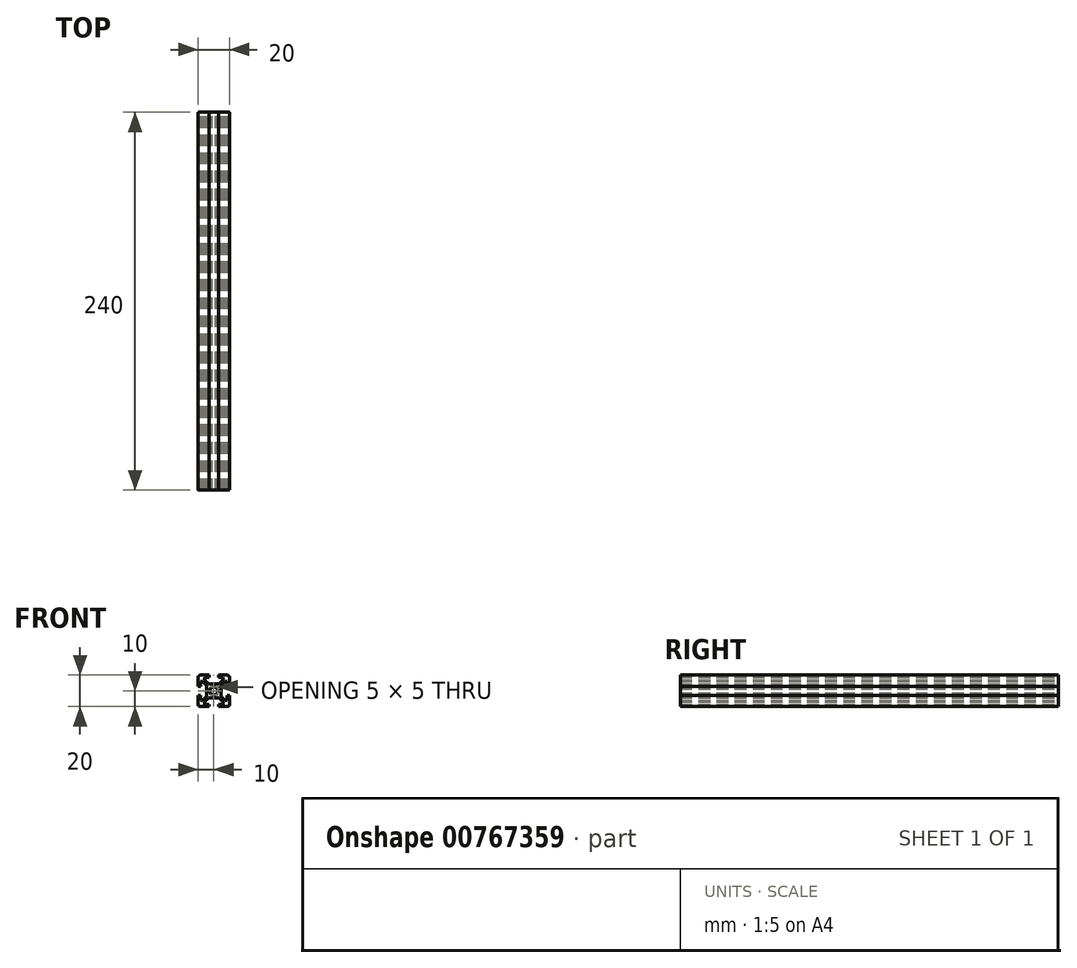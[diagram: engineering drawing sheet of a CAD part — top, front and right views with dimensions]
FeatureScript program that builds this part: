
annotation { "Feature Type Name" : "Feature", "Feature Type Description" : "" }
export const myFeature = defineFeature(function(context is Context, id is Id, definition is map)
    precondition{}
    {
        {
            var Q0;
            Q0=qCreatedBy(makeId("Front.planeOp"),FACE);
            var sketch = newSketch(context, id + "F0", { "sketchPlane" : qUnion([Q0])});
            skLineSegment(sketch, "E0.bottom", {"start": v(8.5, -10) * mm, "end": v(3, -10) * mm});
            skLineSegment(sketch, "E0.top", {"start": v(8.5, 10) * mm, "end": v(3, 10) * mm});
            skLineSegment(sketch, "E0.left", {"start": v(10, -8.5) * mm, "end": v(10, -3) * mm});
            skLineSegment(sketch, "E0.right", {"start": v(-10, -8.5) * mm, "end": v(-10, -3) * mm});
            skPoint(sketch, "E0.middle", {"position": v(0, 0) * mm});
            skLineSegment(sketch, "E1.bottom", {"start": v(6, -8.5) * mm, "end": v(3, -8.5) * mm});
            skLineSegment(sketch, "E1.top", {"start": v(6, 8.5) * mm, "end": v(3, 8.5) * mm});
            skLineSegment(sketch, "E1.left", {"start": v(8.5, -6) * mm, "end": v(8.5, -3) * mm});
            skLineSegment(sketch, "E1.right", {"start": v(-8.5, -6) * mm, "end": v(-8.5, -3) * mm});
            skLineSegment(sketch, "E2.bottom", {"start": v(3.44, -4.5) * mm, "end": v(-3.44, -4.5) * mm});
            skLineSegment(sketch, "E2.top", {"start": v(3.44, 4.5) * mm, "end": v(-3.44, 4.5) * mm});
            skLineSegment(sketch, "E2.left", {"start": v(4.5, -3.44) * mm, "end": v(4.5, 3.44) * mm});
            skLineSegment(sketch, "E2.right", {"start": v(-4.5, -3.44) * mm, "end": v(-4.5, 3.44) * mm});
            skLineSegment(sketch, "E3.bottom", {"start": v(8.5, -6) * mm, "end": v(7.06, -6) * mm});
            skLineSegment(sketch, "E3.top", {"start": v(8.5, 6) * mm, "end": v(7.06, 6) * mm});
            skLineSegment(sketch, "E4.left", {"start": v(6, -8.5) * mm, "end": v(6, -7.06) * mm});
            skLineSegment(sketch, "E4.right", {"start": v(-6, -8.5) * mm, "end": v(-6, -7.06) * mm});
            skPoint(sketch, "E5.orphan", {"position": v(-8.5, 8.5) * mm});
            skPoint(sketch, "E6.orphan", {"position": v(8.5, 8.5) * mm});
            skPoint(sketch, "E7.orphan", {"position": v(8.5, -8.5) * mm});
            skPoint(sketch, "E8.orphan", {"position": v(-8.5, -8.5) * mm});
            skLineSegment(sketch, "E9.trimOffspring", {"start": v(-6, 7.06) * mm, "end": v(-6, 8.5) * mm});
            skLineSegment(sketch, "E10.trimOffspring", {"start": v(-7.06, 6) * mm, "end": v(-8.5, 6) * mm});
            skLineSegment(sketch, "E11.trimOffspring", {"start": v(6, 7.06) * mm, "end": v(6, 8.5) * mm});
            skLineSegment(sketch, "E12.trimOffspring", {"start": v(-7.06, -6) * mm, "end": v(-8.5, -6) * mm});
            skLineSegment(sketch, "E13", {"start": v(-10, 10) * mm, "end": v(0, 0) * mm, "construction": true});
            skLineSegment(sketch, "E14", {"start": v(10, 10) * mm, "end": v(0, 0) * mm, "construction": true});
            skLineSegment(sketch, "E15", {"start": v(-6, 7.06) * mm, "end": v(-3.44, 4.5) * mm});
            skPoint(sketch, "E15.endSnap0", {"position": v(7.25, -6) * mm});
            skLineSegment(sketch, "E16", {"start": v(6, -7.06) * mm, "end": v(3.44, -4.5) * mm});
            skLineSegment(sketch, "E17", {"start": v(7.06, 6) * mm, "end": v(4.5, 3.44) * mm});
            skLineSegment(sketch, "E18", {"start": v(6, 7.06) * mm, "end": v(3.44, 4.5) * mm});
            skPoint(sketch, "E19.orphan", {"position": v(6, -6) * mm});
            skPoint(sketch, "E20.orphan", {"position": v(-4.5, -4.5) * mm});
            skPoint(sketch, "E21.orphan", {"position": v(-4.5, 4.5) * mm});
            skPoint(sketch, "E22.orphan", {"position": v(4.5, 4.5) * mm});
            skPoint(sketch, "E23.orphan", {"position": v(4.5, -4.5) * mm});
            skLineSegment(sketch, "E24.trimOffspring", {"start": v(4.5, -3.44) * mm, "end": v(7.06, -6) * mm});
            skLineSegment(sketch, "E25.trimOffspring", {"start": v(-3.44, -4.5) * mm, "end": v(-6, -7.06) * mm});
            skLineSegment(sketch, "E26.trimOffspring", {"start": v(-4.5, -3.44) * mm, "end": v(-7.06, -6) * mm});
            skLineSegment(sketch, "E27.trimOffspring", {"start": v(-4.5, 3.44) * mm, "end": v(-7.06, 6) * mm});
            skLineSegment(sketch, "E28.bottom", {"start": v(8.5, -3) * mm, "end": v(10, -3) * mm});
            skLineSegment(sketch, "E28.top", {"start": v(8.5, 3) * mm, "end": v(10, 3) * mm});
            skPoint(sketch, "E28.middle", {"position": v(10, 0) * mm});
            skLineSegment(sketch, "E29.left", {"start": v(3, 8.5) * mm, "end": v(3, 10) * mm});
            skLineSegment(sketch, "E29.right", {"start": v(-3, 8.5) * mm, "end": v(-3, 10) * mm});
            skPoint(sketch, "E29.middle", {"position": v(0, 10) * mm});
            skLineSegment(sketch, "E30.bottom", {"start": v(-8.5, 3) * mm, "end": v(-10, 3) * mm});
            skLineSegment(sketch, "E30.top", {"start": v(-8.5, -3) * mm, "end": v(-10, -3) * mm});
            skPoint(sketch, "E30.middle", {"position": v(-10, 0) * mm});
            skLineSegment(sketch, "E31.left", {"start": v(3, -8.5) * mm, "end": v(3, -10) * mm});
            skLineSegment(sketch, "E31.right", {"start": v(-3, -8.5) * mm, "end": v(-3, -10) * mm});
            skPoint(sketch, "E31.middle", {"position": v(0, -10) * mm});
            skPoint(sketch, "E32.orphan", {"position": v(3, 11.5) * mm});
            skPoint(sketch, "E33.orphan", {"position": v(-3, 11.5) * mm});
            skLineSegment(sketch, "E34.trimOffspring", {"start": v(-3, 10) * mm, "end": v(-8.5, 10) * mm});
            skLineSegment(sketch, "E35.trimOffspring", {"start": v(-3, 8.5) * mm, "end": v(-6, 8.5) * mm});
            skPoint(sketch, "E28.right.end.orphan", {"position": v(11.5, 3) * mm});
            skPoint(sketch, "E36.orphan", {"position": v(11.5, -3) * mm});
            skLineSegment(sketch, "E37.trimOffspring", {"start": v(10, 3) * mm, "end": v(10, 8.5) * mm});
            skLineSegment(sketch, "E38.trimOffspring", {"start": v(8.5, 3) * mm, "end": v(8.5, 6) * mm});
            skPoint(sketch, "E39.orphan", {"position": v(3, -11.5) * mm});
            skPoint(sketch, "E40.orphan", {"position": v(-3, -11.5) * mm});
            skLineSegment(sketch, "E41.trimOffspring", {"start": v(-3, -10) * mm, "end": v(-8.5, -10) * mm});
            skLineSegment(sketch, "E42.trimOffspring", {"start": v(-3, -8.5) * mm, "end": v(-6, -8.5) * mm});
            skPoint(sketch, "E30.right.end.orphan", {"position": v(-11.5, -3) * mm});
            skPoint(sketch, "E43.orphan", {"position": v(-11.5, 3) * mm});
            skLineSegment(sketch, "E44.trimOffspring", {"start": v(-10, 3) * mm, "end": v(-10, 8.5) * mm});
            skLineSegment(sketch, "E45.trimOffspring", {"start": v(-8.5, 3) * mm, "end": v(-8.5, 6) * mm});
            skLineSegment(sketch, "E46.trimOffspring", {"start": v(0, 0) * mm, "end": v(10, -10) * mm, "construction": true});
            skLineSegment(sketch, "E47.trimOffspring", {"start": v(0, 0) * mm, "end": v(-10, -10) * mm, "construction": true});
            skArc(sketch, "E48", {"start": v(1.16, 2.22) * mm, "mid": v(0, 2.5) * mm, "end": v(-1.16, 2.22) * mm});
            skLineSegment(sketch, "E49", {"start": v(-2.5, -1.44) * mm, "end": v(1.44, 2.5) * mm});
            skLineSegment(sketch, "E50", {"start": v(2.5, 1.44) * mm, "end": v(-1.44, -2.5) * mm});
            skLineSegment(sketch, "E51", {"start": v(1.44, -2.5) * mm, "end": v(-2.5, 1.44) * mm});
            skLineSegment(sketch, "E52", {"start": v(-1.44, 2.5) * mm, "end": v(2.5, -1.44) * mm});
            skLineSegment(sketch, "E53", {"start": v(2.5, 1.44) * mm, "end": v(2.5, -1.44) * mm, "construction": true});
            skLineSegment(sketch, "E54", {"start": v(1.44, -2.5) * mm, "end": v(-1.44, -2.5) * mm, "construction": true});
            skLineSegment(sketch, "E55", {"start": v(-2.5, -1.44) * mm, "end": v(-2.5, 1.44) * mm, "construction": true});
            skLineSegment(sketch, "E56", {"start": v(-1.44, 2.5) * mm, "end": v(1.44, 2.5) * mm, "construction": true});
            skLineSegment(sketch, "E57", {"start": v(-1.44, 2.5) * mm, "end": v(-2.5, 1.44) * mm});
            skLineSegment(sketch, "E58", {"start": v(1.44, 2.5) * mm, "end": v(2.5, 1.44) * mm});
            skLineSegment(sketch, "E59", {"start": v(2.5, -1.44) * mm, "end": v(1.44, -2.5) * mm});
            skLineSegment(sketch, "E60", {"start": v(-1.44, -2.5) * mm, "end": v(-2.5, -1.44) * mm});
            skArc(sketch, "E61.trimOffspring", {"start": v(-2.22, 1.16) * mm, "mid": v(-2.5, 0) * mm, "end": v(-2.22, -1.16) * mm});
            skArc(sketch, "E62.trimOffspring", {"start": v(-1.16, -2.22) * mm, "mid": v(0, -2.5) * mm, "end": v(1.16, -2.22) * mm});
            skArc(sketch, "E63.trimOffspring", {"start": v(2.22, -1.16) * mm, "mid": v(2.5, 0) * mm, "end": v(2.22, 1.16) * mm});
            skPoint(sketch, "E64.visualSharp", {"position": v(10, 10) * mm});
            skArc(sketch, "E64.filletArc", {"start": v(10, 8.5) * mm, "mid": v(9.56, 9.56) * mm, "end": v(8.5, 10) * mm});
            skPoint(sketch, "E65.visualSharp", {"position": v(10, -10) * mm});
            skArc(sketch, "E65.filletArc", {"start": v(8.5, -10) * mm, "mid": v(9.56, -9.56) * mm, "end": v(10, -8.5) * mm});
            skPoint(sketch, "E66.visualSharp", {"position": v(-10, -10) * mm});
            skArc(sketch, "E66.filletArc", {"start": v(-10, -8.5) * mm, "mid": v(-9.56, -9.56) * mm, "end": v(-8.5, -10) * mm});
            skPoint(sketch, "E67.visualSharp", {"position": v(-10, 10) * mm});
            skArc(sketch, "E67.filletArc", {"start": v(-8.5, 10) * mm, "mid": v(-9.56, 9.56) * mm, "end": v(-10, 8.5) * mm});
            skSolve(sketch);
        }
        {
            assignVariable(context, id + "F2", {"name" : "Length", "anyValue" : 240});
        }
        {
            var Q0;
            Q0=qSketchRegion(id+"F0",true);
            extrude(context, id + "F1", {"entities" : qUnion([Q0]), "depth" : (getVariable(context, 'Length')) * mm});
        }
    });
